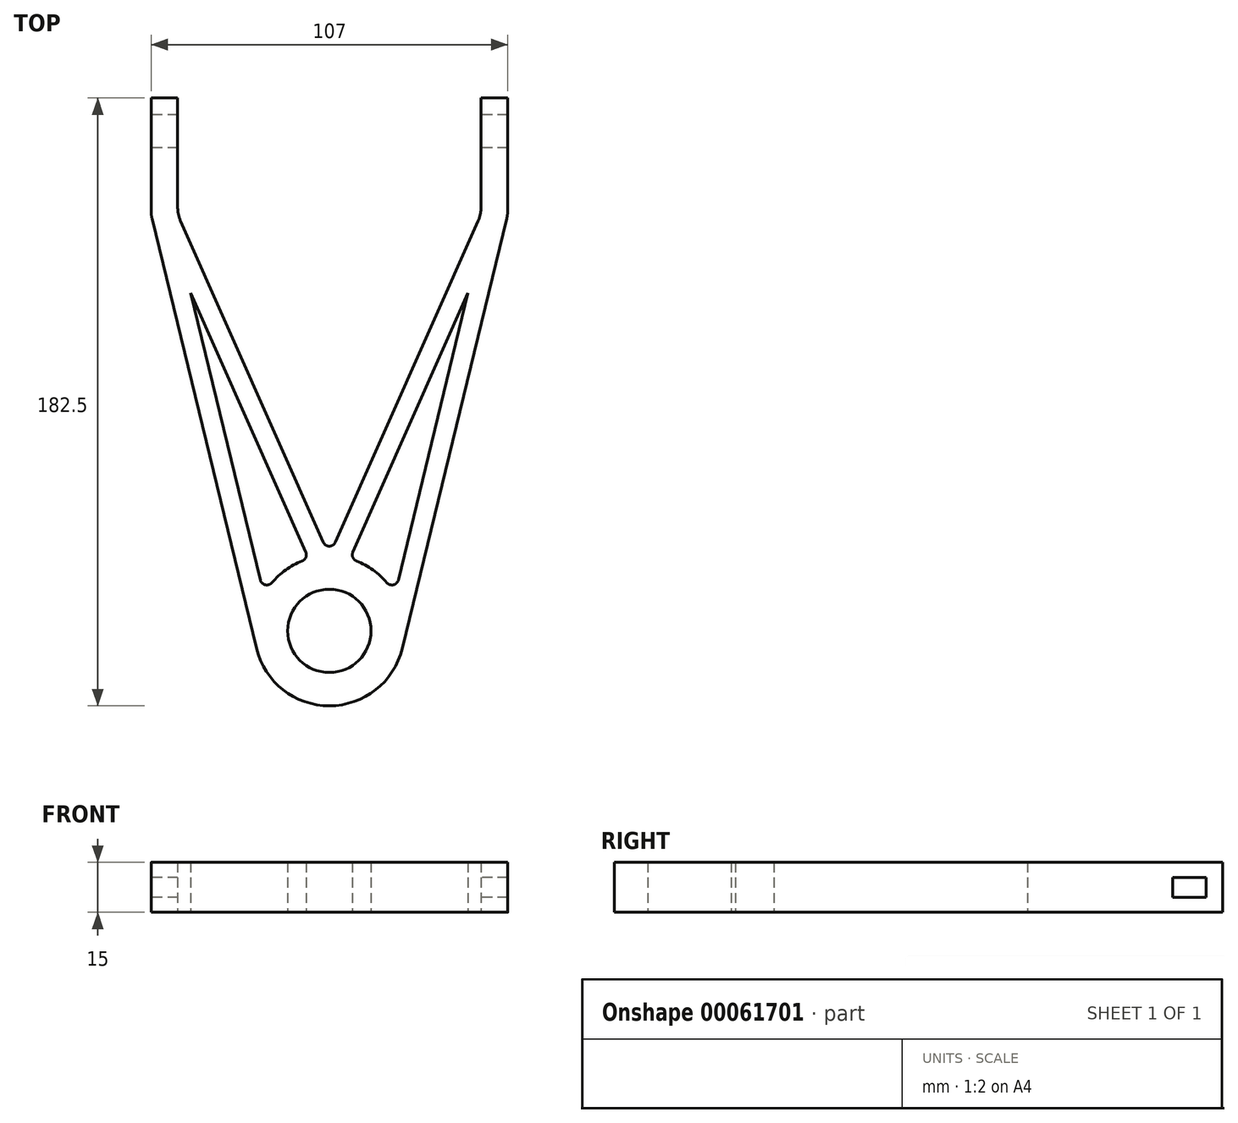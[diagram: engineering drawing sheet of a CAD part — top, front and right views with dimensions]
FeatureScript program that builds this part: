
annotation { "Feature Type Name" : "Feature", "Feature Type Description" : "" }
export const myFeature = defineFeature(function(context is Context, id is Id, definition is map)
    precondition{}
    {
        {
            var Q0;
            Q0=qCreatedBy(makeId("Top.planeOp"),FACE);
            var sketch = newSketch(context, id + "F0", { "sketchPlane" : qUnion([Q0])});
            skCircle(sketch, "E0", {"center": v(0, 0) * mm, "radius": 12.5 * mm});
            skCircle(sketch, "E1", {"center": v(0, 0) * mm, "radius": 22.5 * mm});
            skLineSegment(sketch, "E2", {"start": v(-21.86, -5.3) * mm, "end": v(-53.5, 125) * mm});
            skLineSegment(sketch, "E3", {"start": v(-53.5, 125) * mm, "end": v(-53.5, 160) * mm});
            skLineSegment(sketch, "E4", {"start": v(-53.5, 160) * mm, "end": v(-45.5, 160) * mm});
            skLineSegment(sketch, "E5", {"start": v(-45.5, 160) * mm, "end": v(-45.5, 125) * mm});
            skLineSegment(sketch, "E6", {"start": v(-45.5, 125) * mm, "end": v(0, 22.5) * mm});
            skLineSegment(sketch, "E7.MirrorCS", {"start": v(21.86, -5.3) * mm, "end": v(53.5, 125) * mm});
            skLineSegment(sketch, "E8.MirrorCS", {"start": v(53.5, 125) * mm, "end": v(53.5, 160) * mm});
            skLineSegment(sketch, "E9.MirrorCS", {"start": v(53.5, 160) * mm, "end": v(45.5, 160) * mm});
            skLineSegment(sketch, "E10.MirrorCS", {"start": v(45.5, 160) * mm, "end": v(45.5, 125) * mm});
            skLineSegment(sketch, "E11.MirrorCS", {"start": v(45.5, 125) * mm, "end": v(0, 22.5) * mm});
            skLineSegment(sketch, "E12", {"start": v(-41.6, 101.44) * mm, "end": v(-19.64, 10.97) * mm});
            skLineSegment(sketch, "E13", {"start": v(-6.18, 21.63) * mm, "end": v(-41.6, 101.44) * mm});
            skLineSegment(sketch, "E14.MirrorCS", {"start": v(6.18, 21.63) * mm, "end": v(41.6, 101.44) * mm});
            skLineSegment(sketch, "E15.MirrorCS", {"start": v(41.6, 101.44) * mm, "end": v(19.64, 10.97) * mm});
            skSolve(sketch);
        }
        {
            var Q0;
            Q0 = qSketchRegion(id + "F0", true);
            extrude(context, id + "F1", {"entities" : qUnion([Q0]), "depth" : 15 * mm});
        }
        {
            var Q0;
            Q0=makeQuery(id+"F1.opExtrude","SWEPT_EDGE",EDGE,{"disambiguationData":[OSD([sQuery(id+"F0.wireOp",EDGE,"E2"),sQuery(id+"F0.wireOp",EDGE,"E3")])]});
            var Q1;
            Q1=makeQuery(id+"F1.opExtrude","SWEPT_EDGE",EDGE,{"disambiguationData":[OSD([sQuery(id+"F0.wireOp",EDGE,"E10.MirrorCS"),sQuery(id+"F0.wireOp",EDGE,"E11.MirrorCS")])]});
            var Q2;
            Q2=makeQuery(id+"F1.opExtrude","SWEPT_EDGE",EDGE,{"disambiguationData":[OSD([sQuery(id+"F0.wireOp",EDGE,"E5"),sQuery(id+"F0.wireOp",EDGE,"E6")])]});
            var Q3;
            Q3=makeQuery(id+"F1.opExtrude","SWEPT_EDGE",EDGE,{"disambiguationData":[OSD([sQuery(id+"F0.wireOp",EDGE,"E7.MirrorCS"),sQuery(id+"F0.wireOp",EDGE,"E8.MirrorCS")])]});
            fillet(context, id + "F2", {"entities" : qUnion([Q0, Q1, Q2, Q3]), "radius" : 10 * mm, "tangentPropagation" : true, "allowEdgeOverflow" : false});
        }
        {
            var Q0;
            Q0=makeQuery(id+"F1.opExtrude","SWEPT_EDGE",EDGE,{"disambiguationData":[OSD([sQuery(id+"F0.wireOp",EDGE,"E1"),sQuery(id+"F0.wireOp",EDGE,"E13")])]});
            var Q1;
            Q1=makeQuery(id+"F1.opExtrude","SWEPT_EDGE",EDGE,{"disambiguationData":[OSD([sQuery(id+"F0.wireOp",EDGE,"E1"),sQuery(id+"F0.wireOp",EDGE,"E12")])]});
            var Q2;
            Q2=makeQuery(id+"F1.opExtrude","SWEPT_EDGE",EDGE,{"disambiguationData":[OSD([sQuery(id+"F0.wireOp",EDGE,"E1"),sQuery(id+"F0.wireOp",EDGE,"E15.MirrorCS")])]});
            var Q3;
            Q3=makeQuery(id+"F1.opExtrude","SWEPT_EDGE",EDGE,{"disambiguationData":[OSD([sQuery(id+"F0.wireOp",EDGE,"E1"),sQuery(id+"F0.wireOp",EDGE,"E14.MirrorCS")])]});
            var Q4;
            Q4=makeQuery(id+"F1.opExtrude","SWEPT_EDGE",EDGE,{"disambiguationData":[OSD([sQuery(id+"F0.wireOp",EDGE,"E1"),sQuery(id+"F0.wireOp",EDGE,"E6"),sQuery(id+"F0.wireOp",EDGE,"E11.MirrorCS")])]});
            fillet(context, id + "F3", {"entities" : qUnion([Q0, Q1, Q2, Q3, Q4]), "radius" : 2 * mm, "tangentPropagation" : true, "allowEdgeOverflow" : false});
        }
        {
            var Q0;
            Q0=makeQuery(id+"F1.opExtrude","SWEPT_FACE",FACE,{"disambiguationData":[OSD([sQuery(id+"F0.wireOp",EDGE,"E3")])]});
            var sketch = newSketch(context, id + "F4", { "sketchPlane" : qUnion([Q0])});
            skLineSegment(sketch, "E16.bottom", {"start": v(-155, 4.5) * mm, "end": v(-145, 4.5) * mm});
            skLineSegment(sketch, "E16.top", {"start": v(-155, 10.5) * mm, "end": v(-145, 10.5) * mm});
            skLineSegment(sketch, "E16.left", {"start": v(-155, 4.5) * mm, "end": v(-155, 10.5) * mm});
            skLineSegment(sketch, "E16.right", {"start": v(-145, 4.5) * mm, "end": v(-145, 10.5) * mm});
            skSolve(sketch);
        }
        {
            var Q0;
            Q0 = qSketchRegion(id + "F4", true);
            extrude(context, id + "F5", {"entities" : qUnion([Q0]), "operationType" : NewBodyOperationType.REMOVE, "endBound" : BoundingType.THROUGH_ALL, "oppositeDirection" : true, "depth" : 25 * mm});
        }
    });
